# Revit family: Baie Linkeo DC largeur 600
name_source: partatom
category: Equipement spécialisé
units: mm (PartAtom-declared; Revit-internal decimal feet)

## family parameters
Basée sur le plan de construction = Non
Cote de connecteur circulaire = Utiliser le diamètre
Couper avec des vides une fois chargée = Non
Partagée = Oui
Point de calcul de pièce = Non
Toujours verticalement = Oui
Type d'élément = Normal

## types (4) — shared parameters
Avec mise à la terre = Oui
Avec porte frontale = Oui
Avec tôle de toit = Oui
Capacité de charge max = 1500
Classe d'application = EC002499
Couleur = IDS_NOIR
Dimension modulaire = 19 pouces
Distance ouverture 1 = 275 mm
Emplacement de rack = 93 mm  [stored 0.305118 ft]
Finition de surface = Poudré
Finition du rail profilé = Recourbée
Fonction = Baies serveur Linkeo DC
Indice de protection IK = IK02
Indice de protection IP = IP20
Largeur (mm) = 600 mm
Lien e-catalogue = https://www.legrand.fr
Matériau = Acier
Matériau de la porte avant = IDS_ACIER
Modèle = Corps fixe
Modèle de largeur = 600 mm
Nombre de portes = 1
Passage utile en hauteur (mm) = 1881 mm  [stored 6.17126 ft]
RAL = 9005
Température de fonctionnement = -25°C à 70°C
Température de stockage = -25°C à 70°C
Type d'aération = Passive
Type de montage = Avant et arrière
Verrouillage de la porte avant = A trois points
zero-valued in all types: Elévation par défaut

## per-type parameters (varying)
| type | Hauteur | Hauteur du modèle | Libellé BIM | Nombre d'unités en hauteur | Passage utile en largeur (mm) | Profondeur | Profondeur du modèle | Référence Legrand |
| Baie Linkeo2 42U 600x1000 | 2047 mm  [stored 6.71588 ft] | 1965 mm  [stored 6.44685 ft] | Baie Linkeo DC 42U 600x1000 équipée | 42 | 890 mm  [stored 2.91995 ft] | 1000 mm  [stored 3.28084 ft] | 1000 mm  [stored 3.28084 ft] | 446800 |
| Baie Linkeo2 42U 600x1200 | 2047 mm  [stored 6.71588 ft] | 1965 mm  [stored 6.44685 ft] | Baie Linkeo DC 42U 600x1200 équipée | 42 | 1090 mm  [stored 3.57612 ft] | 1200 mm | 1200 mm | 446801 |
| Baie Linkeo2 47U 600x1000 | 2269 mm | 2190 mm  [stored 7.18504 ft] | Baie Linkeo DC 47U 600x1000 équipée | 47 | 890 mm  [stored 2.91995 ft] | 1000 mm  [stored 3.28084 ft] | 1000 mm  [stored 3.28084 ft] | 446804 |
| Baie Linkeo2 47U 600x1200 | 2269 mm | 2190 mm  [stored 7.18504 ft] | Baie Linkeo DC 47U 600x1200 équipée | 47 | 1090 mm  [stored 3.57612 ft] | 1200 mm | 1200 mm | 446805 |

note: [stored X ft] marks values corroborated as IEEE doubles in the binary element streams (Revit-internal decimal feet)
